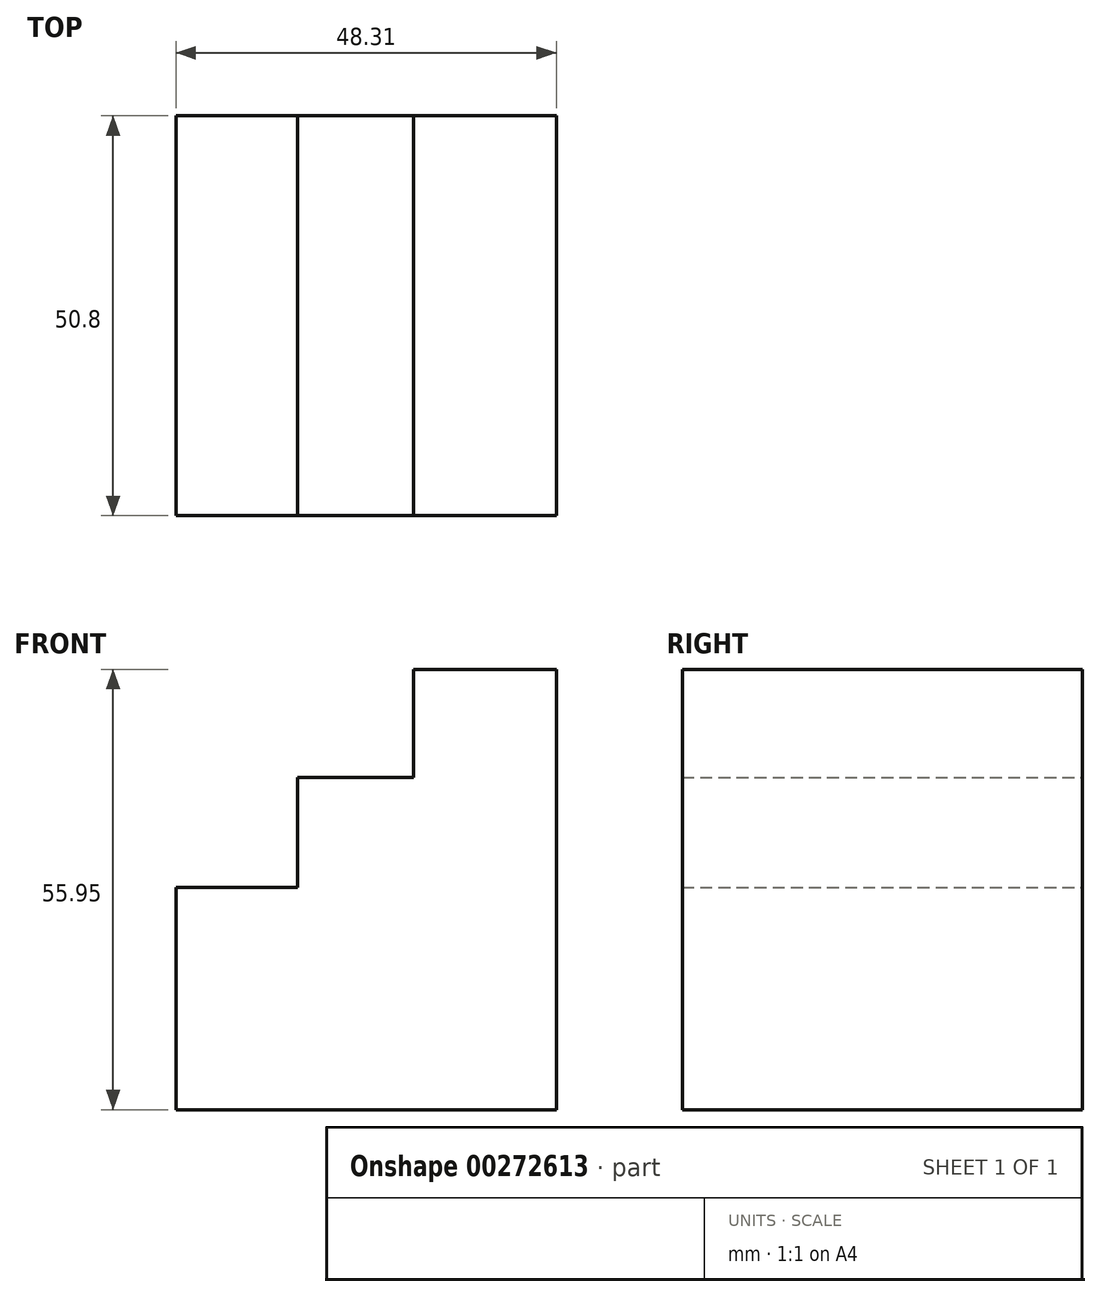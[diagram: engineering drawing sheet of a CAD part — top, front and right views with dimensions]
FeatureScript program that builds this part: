
annotation { "Feature Type Name" : "Feature", "Feature Type Description" : "" }
export const myFeature = defineFeature(function(context is Context, id is Id, definition is map)
    precondition{}
    {
        {
            var Q0;
            Q0=qCreatedBy(makeId("Front.planeOp"),FACE);
            var sketch = newSketch(context, id + "F0", { "sketchPlane" : qUnion([Q0])});
            skLineSegment(sketch, "E0", {"start": v(0, 55.95) * mm, "end": v(0, 0) * mm});
            skLineSegment(sketch, "E1", {"start": v(0, 55.95) * mm, "end": v(-18.14, 55.95) * mm});
            skLineSegment(sketch, "E2", {"start": v(-18.14, 55.95) * mm, "end": v(-18.14, 42.2) * mm});
            skLineSegment(sketch, "E3", {"start": v(-18.14, 42.2) * mm, "end": v(-32.84, 42.2) * mm});
            skLineSegment(sketch, "E4", {"start": v(-32.84, 42.2) * mm, "end": v(-32.84, 28.26) * mm});
            skLineSegment(sketch, "E5", {"start": v(-32.65, 28.26) * mm, "end": v(-48.31, 28.26) * mm});
            skLineSegment(sketch, "E6", {"start": v(-48.31, 28.26) * mm, "end": v(-48.31, 0) * mm});
            skLineSegment(sketch, "E7", {"start": v(0, 0) * mm, "end": v(-48.31, 0) * mm});
            skSolve(sketch);
        }
        {
            var Q0;
            Q0 = qSketchRegion(id + "F0", true);
            extrude(context, id + "F1", {"entities" : qUnion([Q0]), "depth" : 50.8 * mm});
        }
    });
